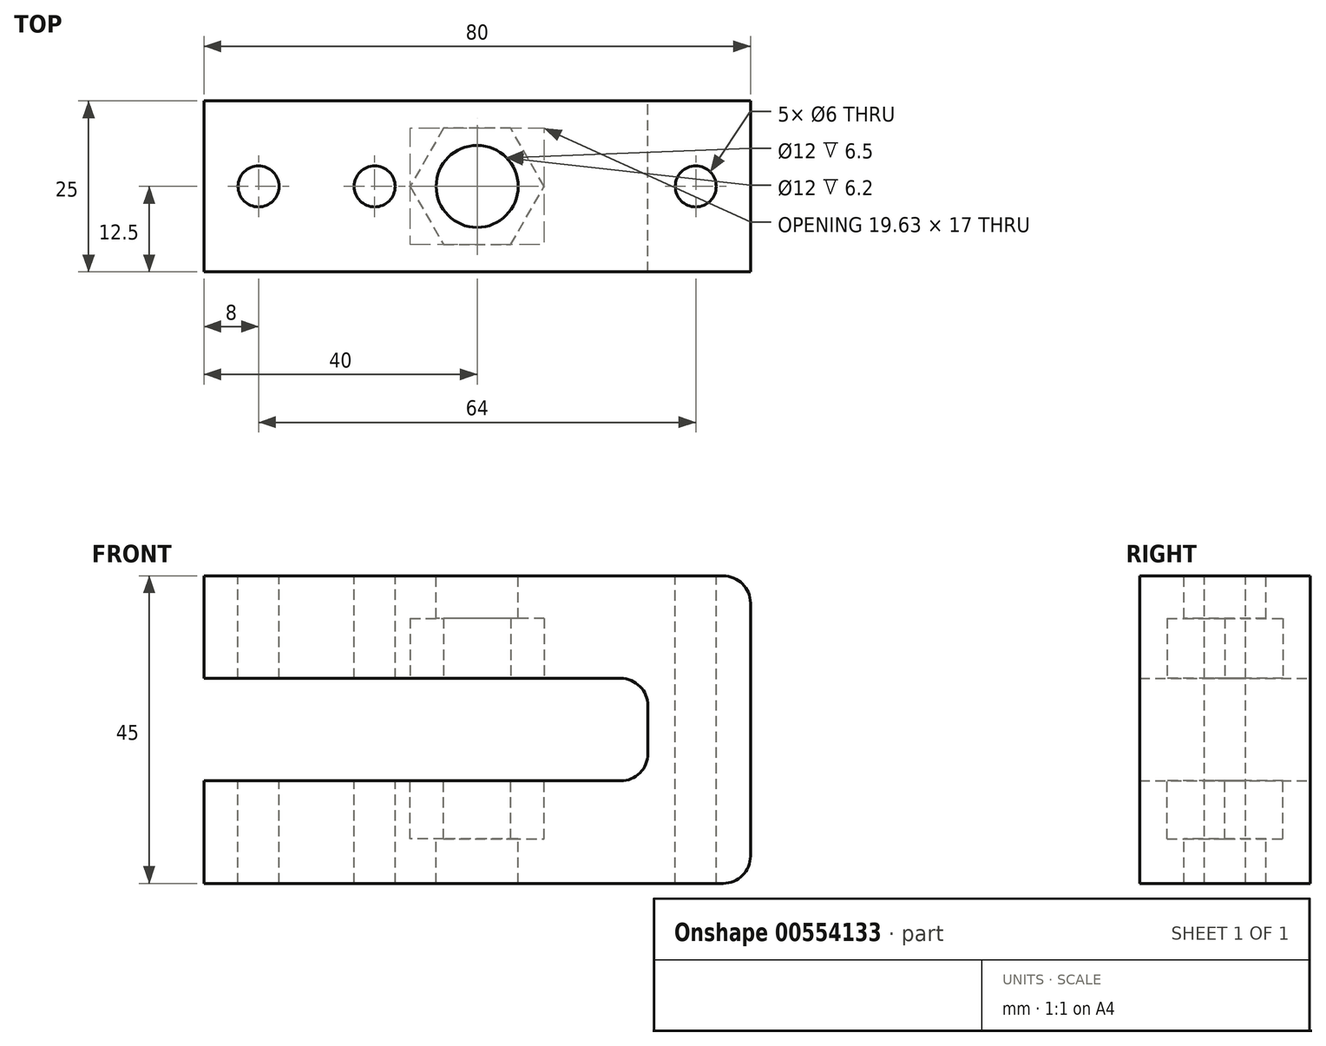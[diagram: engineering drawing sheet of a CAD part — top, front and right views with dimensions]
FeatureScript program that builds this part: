
annotation { "Feature Type Name" : "Feature", "Feature Type Description" : "" }
export const myFeature = defineFeature(function(context is Context, id is Id, definition is map)
    precondition{}
    {
        {
            var Q0;
            Q0=qCreatedBy(makeId("Front.planeOp"),FACE);
            var sketch = newSketch(context, id + "F0", { "sketchPlane" : qUnion([Q0])});
            skLineSegment(sketch, "E0.bottom", {"start": v(0, 0) * mm, "end": v(80, 0) * mm});
            skLineSegment(sketch, "E0.top", {"start": v(0, 45) * mm, "end": v(80, 45) * mm});
            skLineSegment(sketch, "E0.left", {"start": v(0, 0) * mm, "end": v(0, 15) * mm});
            skLineSegment(sketch, "E0.right", {"start": v(80, 0) * mm, "end": v(80, 45) * mm});
            skLineSegment(sketch, "E1.bottom", {"start": v(0, 15) * mm, "end": v(65, 15) * mm});
            skLineSegment(sketch, "E1.top", {"start": v(0, 30) * mm, "end": v(65, 30) * mm});
            skLineSegment(sketch, "E1.right", {"start": v(65, 15) * mm, "end": v(65, 30) * mm});
            skLineSegment(sketch, "E2.trimOffspring", {"start": v(0, 30) * mm, "end": v(0, 45) * mm});
            skSolve(sketch);
        }
        {
            var Q0;
            Q0=makeQuery(id+"F0.imprint","IMPRINT",FACE,{"disambiguationData":[TD([[makeQuery(id+"F0.imprint","IMPRINT",EDGE,{"derivedFrom":sQuery(id+"F0.wireOp",EDGE,"E0.bottom")}),1.0]])]});
            extrude(context, id + "F1", {"entities" : qUnion([Q0]), "depth" : 25 * mm, "offsetDistance" : 25 * mm});
        }
        {
            var Q0;
            Q0=makeQuery(id+"F1.opExtrude","SWEPT_FACE",FACE,{"disambiguationData":[OSD([sQuery(id+"F0.wireOp",EDGE,"E0.top")])]});
            var sketch = newSketch(context, id + "F2", { "sketchPlane" : qUnion([Q0])});
            skCircle(sketch, "E3", {"center": v(40, -12.5) * mm, "radius": 6 * mm});
            skPoint(sketch, "E3.centerSnap0", {"position": v(80, -12.5) * mm});
            skPoint(sketch, "E3.centerSnap1", {"position": v(40, 0) * mm});
            skCircle(sketch, "E4", {"center": v(8, -12.5) * mm, "radius": 3 * mm});
            skPoint(sketch, "E4.centerSnap0", {"position": v(0, -12.5) * mm});
            skCircle(sketch, "E5", {"center": v(25, -12.5) * mm, "radius": 3 * mm});
            skCircle(sketch, "E6", {"center": v(72, -12.5) * mm, "radius": 3 * mm});
            skSolve(sketch);
        }
        {
            var Q0;
            Q0=makeQuery(id+"F2.imprint","IMPRINT",FACE,{"disambiguationData":[TD([[makeQuery(id+"F2.imprint","IMPRINT",EDGE,{"derivedFrom":sQuery(id+"F2.wireOp",EDGE,"E3")}),1.0]])]});
            var Q1;
            Q1=makeQuery(id+"F2.imprint","IMPRINT",FACE,{"disambiguationData":[TD([[makeQuery(id+"F2.imprint","IMPRINT",EDGE,{"derivedFrom":sQuery(id+"F2.wireOp",EDGE,"E4")}),1.0]])]});
            var Q2;
            Q2=makeQuery(id+"F2.imprint","IMPRINT",FACE,{"disambiguationData":[TD([[makeQuery(id+"F2.imprint","IMPRINT",EDGE,{"derivedFrom":sQuery(id+"F2.wireOp",EDGE,"E5")}),1.0]])]});
            var Q3;
            Q3=makeQuery(id+"F2.imprint","IMPRINT",FACE,{"disambiguationData":[TD([[makeQuery(id+"F2.imprint","IMPRINT",EDGE,{"derivedFrom":sQuery(id+"F2.wireOp",EDGE,"E6")}),1.0]])]});
            extrude(context, id + "F3", {"entities" : qUnion([Q0, Q1, Q2, Q3]), "operationType" : NewBodyOperationType.REMOVE, "endBound" : BoundingType.THROUGH_ALL, "oppositeDirection" : true, "depth" : 25 * mm, "offsetDistance" : 25 * mm});
        }
        {
            var Q0;
            Q0=makeQuery(id+"F1.opExtrude","SWEPT_FACE",FACE,{"disambiguationData":[OSD([sQuery(id+"F0.wireOp",EDGE,"E1.top")])]});
            var sketch = newSketch(context, id + "F4", { "sketchPlane" : qUnion([Q0])});
            skCircle(sketch, "E7.cCircle", {"center": v(40, 12.5) * mm, "radius": 8.5 * mm, "construction": true});
            skLineSegment(sketch, "E7.0", {"start": v(44.9, 4) * mm, "end": v(35.1, 4) * mm});
            skLineSegment(sketch, "E7.1", {"start": v(35.1, 4) * mm, "end": v(30.19, 12.5) * mm});
            skLineSegment(sketch, "E7.2", {"start": v(30.19, 12.5) * mm, "end": v(35.1, 21) * mm});
            skLineSegment(sketch, "E7.3", {"start": v(35.1, 21) * mm, "end": v(44.9, 21) * mm});
            skLineSegment(sketch, "E7.4", {"start": v(44.9, 21) * mm, "end": v(49.81, 12.5) * mm});
            skLineSegment(sketch, "E7.5", {"start": v(49.81, 12.5) * mm, "end": v(44.9, 4) * mm});
            skPoint(sketch, "E7.0.midPoint", {"position": v(40, 4) * mm});
            skSolve(sketch);
        }
        {
            var Q0;
            Q0=makeQuery(id+"F4.imprint","IMPRINT",FACE,{"disambiguationData":[TD([[makeQuery(id+"F4.imprint","IMPRINT",EDGE,{"derivedFrom":sQuery(id+"F4.wireOp",EDGE,"E7.0")}),-1.0]])]});
            extrude(context, id + "F5", {"entities" : qUnion([Q0]), "operationType" : NewBodyOperationType.REMOVE, "oppositeDirection" : true, "depth" : 8.8 * mm, "offsetDistance" : 25 * mm});
        }
        {
            var Q0;
            Q0=makeQuery(id+"F1.opExtrude","SWEPT_FACE",FACE,{"disambiguationData":[OSD([sQuery(id+"F0.wireOp",EDGE,"E1.bottom")])]});
            var sketch = newSketch(context, id + "F6", { "sketchPlane" : qUnion([Q0])});
            skLineSegment(sketch, "E8.0", {"start": v(44.9, -21) * mm, "end": v(49.81, -12.5) * mm});
            skLineSegment(sketch, "E9.0", {"start": v(35.1, -21) * mm, "end": v(44.9, -21) * mm});
            skLineSegment(sketch, "E10.0", {"start": v(30.19, -12.5) * mm, "end": v(35.1, -21) * mm});
            skLineSegment(sketch, "E11.0", {"start": v(35.1, -4) * mm, "end": v(30.19, -12.5) * mm});
            skLineSegment(sketch, "E12.0", {"start": v(44.9, -4) * mm, "end": v(35.1, -4) * mm});
            skLineSegment(sketch, "E13.0", {"start": v(49.81, -12.5) * mm, "end": v(44.9, -4) * mm});
            skSolve(sketch);
        }
        {
            var Q0;
            Q0=makeQuery(id+"F6.imprint","IMPRINT",FACE,{"disambiguationData":[TD([[makeQuery(id+"F6.imprint","IMPRINT",EDGE,{"derivedFrom":sQuery(id+"F6.wireOp",EDGE,"E8.0")}),1.0]])]});
            extrude(context, id + "F7", {"entities" : qUnion([Q0]), "operationType" : NewBodyOperationType.REMOVE, "oppositeDirection" : true, "depth" : 8.5 * mm, "offsetDistance" : 25 * mm});
        }
        {
            var Q0;
            Q0=makeQuery(id+"F1.opExtrude","SWEPT_EDGE",EDGE,{"disambiguationData":[OSD([sQuery(id+"F0.wireOp",EDGE,"E0.top"),sQuery(id+"F0.wireOp",EDGE,"E0.right")])]});
            var Q1;
            Q1=makeQuery(id+"F1.opExtrude","SWEPT_EDGE",EDGE,{"disambiguationData":[OSD([sQuery(id+"F0.wireOp",EDGE,"E0.bottom"),sQuery(id+"F0.wireOp",EDGE,"E0.right")])]});
            var Q2;
            Q2=makeQuery(id+"F1.opExtrude","SWEPT_EDGE",EDGE,{"disambiguationData":[OSD([sQuery(id+"F0.wireOp",EDGE,"E1.top"),sQuery(id+"F0.wireOp",EDGE,"E1.right")])]});
            var Q3;
            Q3=makeQuery(id+"F1.opExtrude","SWEPT_EDGE",EDGE,{"disambiguationData":[OSD([sQuery(id+"F0.wireOp",EDGE,"E1.bottom"),sQuery(id+"F0.wireOp",EDGE,"E1.right")])]});
            fillet(context, id + "F8", {"entities" : qUnion([Q0, Q1, Q2, Q3]), "radius" : 4 * mm, "tangentPropagation" : true, "allowEdgeOverflow" : false});
        }
    });
